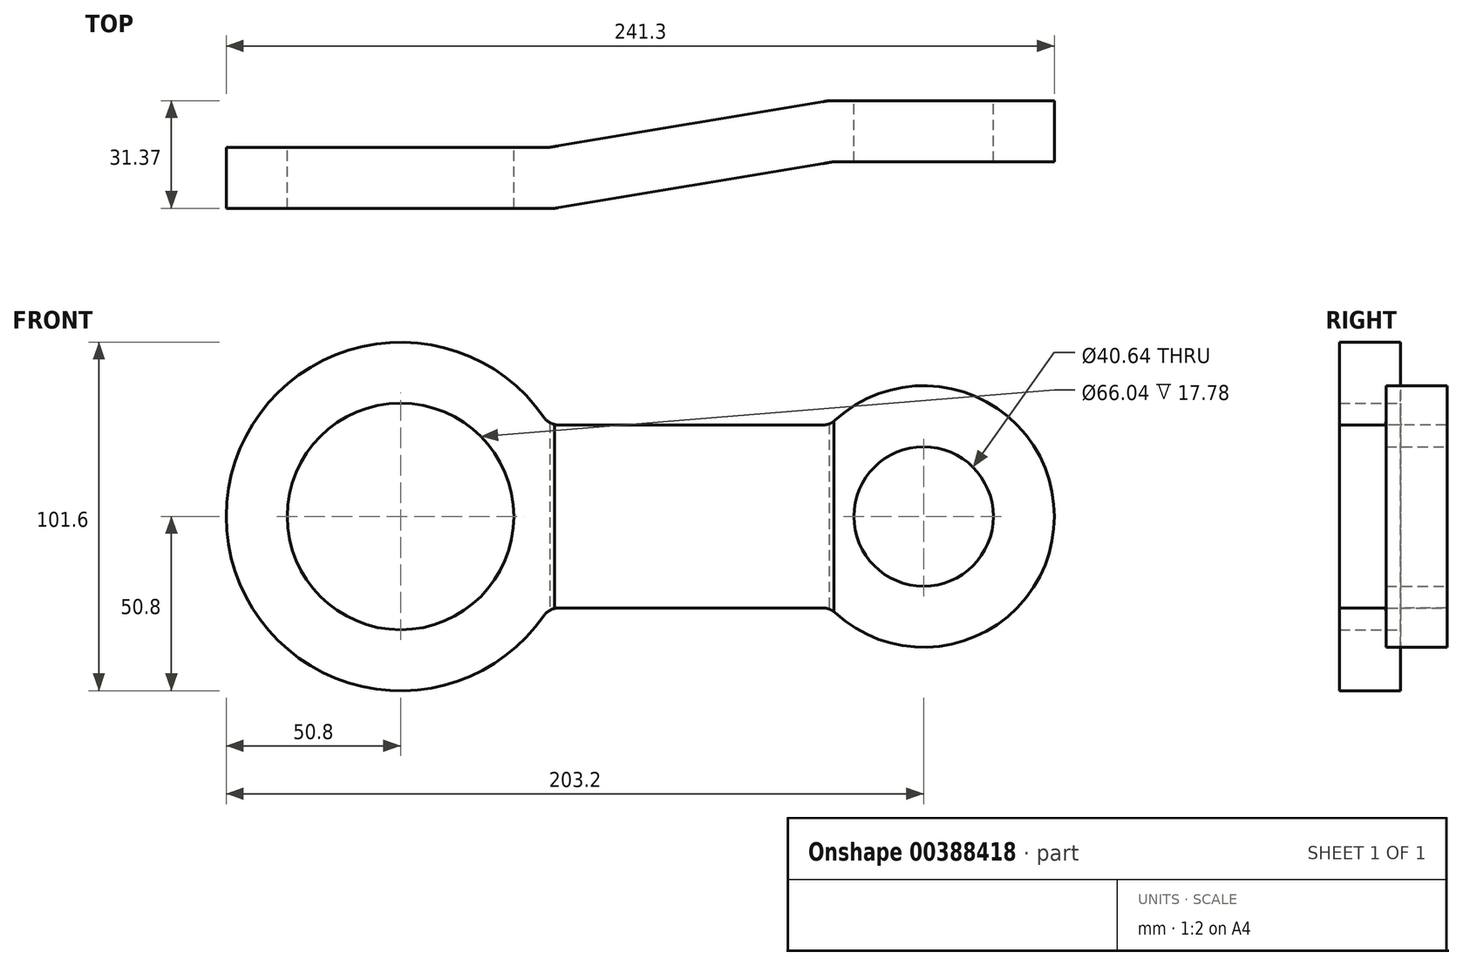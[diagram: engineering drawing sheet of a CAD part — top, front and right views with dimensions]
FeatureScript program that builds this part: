
annotation { "Feature Type Name" : "Feature", "Feature Type Description" : "" }
export const myFeature = defineFeature(function(context is Context, id is Id, definition is map)
    precondition{}
    {
        {
            var Q0;
            Q0=qCreatedBy(makeId("Front.planeOp"),FACE);
            var sketch = newSketch(context, id + "F0", { "sketchPlane" : qUnion([Q0])});
            skCircle(sketch, "E0", {"center": v(0, 0) * mm, "radius": 50.8 * mm});
            skCircle(sketch, "E1", {"center": v(152.4, 0) * mm, "radius": 38.1 * mm});
            skLineSegment(sketch, "E2", {"start": v(152.4, 0) * mm, "end": v(0, 0) * mm, "construction": true});
            skLineSegment(sketch, "E3", {"start": v(125.2, 26.67) * mm, "end": v(43.24, 26.67) * mm});
            skLineSegment(sketch, "E4.MirrorCS", {"start": v(125.2, -26.67) * mm, "end": v(43.24, -26.67) * mm});
            skCircle(sketch, "E5.0", {"center": v(152.4, 0) * mm, "radius": 20.32 * mm});
            skCircle(sketch, "E6.0", {"center": v(0, 0) * mm, "radius": 33.02 * mm});
            skSolve(sketch);
        }
        {
            var Q0;
            Q0 = qSketchRegion(id + "F0", true);
            extrude(context, id + "F1", {"entities" : qUnion([Q0]), "depth" : 50.8 * mm});
        }
        {
            var Q0;
            Q0=qCreatedBy(makeId("Top.planeOp"),FACE);
            var sketch = newSketch(context, id + "F2", { "sketchPlane" : qUnion([Q0])});
            skLineSegment(sketch, "E7", {"start": v(213.7, 0) * mm, "end": v(124.8, 0) * mm});
            skLineSegment(sketch, "E8", {"start": v(124.8, 0) * mm, "end": v(43.44, -13.59) * mm});
            skLineSegment(sketch, "E9", {"start": v(43.44, -13.59) * mm, "end": v(-83.56, -13.59) * mm});
            skLineSegment(sketch, "E10.0", {"start": v(44.92, -31.37) * mm, "end": v(-83.56, -31.37) * mm});
            skLineSegment(sketch, "E10.1", {"start": v(126.28, -17.78) * mm, "end": v(44.92, -31.37) * mm});
            skLineSegment(sketch, "E10.2", {"start": v(213.7, -17.78) * mm, "end": v(126.28, -17.78) * mm});
            skLineSegment(sketch, "E11", {"start": v(213.7, 0) * mm, "end": v(213.7, -17.78) * mm});
            skLineSegment(sketch, "E12", {"start": v(-83.56, -13.59) * mm, "end": v(-83.56, -31.37) * mm});
            skSolve(sketch);
        }
        {
            var Q0;
            Q0 = qSketchRegion(id + "F2", true);
            extrude(context, id + "F3", {"entities" : qUnion([Q0]), "operationType" : NewBodyOperationType.INTERSECT, "endBound" : BoundingType.SYMMETRIC, "depth" : 101.6 * mm});
        }
        {
            var Q0;
            Q0=makeQuery(id+"F1.opExtrude","SWEPT_EDGE",EDGE,{"disambiguationData":[OSD([sQuery(id+"F0.wireOp",EDGE,"E0"),sQuery(id+"F0.wireOp",EDGE,"E3")])]});
            fillet(context, id + "F4", {"entities" : qUnion([Q0]), "radius" : 5.08 * mm, "tangentPropagation" : true, "allowEdgeOverflow" : false});
        }
        {
            var Q0;
            Q0=makeQuery(id+"F1.opExtrude","SWEPT_EDGE",EDGE,{"disambiguationData":[OSD([sQuery(id+"F0.wireOp",EDGE,"E1"),sQuery(id+"F0.wireOp",EDGE,"E3")])]});
            fillet(context, id + "F5", {"entities" : qUnion([Q0]), "radius" : 5.08 * mm, "tangentPropagation" : true, "allowEdgeOverflow" : false});
        }
        {
            var Q0;
            Q0=makeQuery(id+"F1.opExtrude","SWEPT_EDGE",EDGE,{"disambiguationData":[OSD([sQuery(id+"F0.wireOp",EDGE,"E0"),sQuery(id+"F0.wireOp",EDGE,"E4.MirrorCS")])]});
            fillet(context, id + "F6", {"entities" : qUnion([Q0]), "radius" : 5.08 * mm, "tangentPropagation" : true, "allowEdgeOverflow" : false});
        }
        {
            var Q0;
            Q0=makeQuery(id+"F1.opExtrude","SWEPT_EDGE",EDGE,{"disambiguationData":[OSD([sQuery(id+"F0.wireOp",EDGE,"E1"),sQuery(id+"F0.wireOp",EDGE,"E4.MirrorCS")])]});
            fillet(context, id + "F7", {"entities" : qUnion([Q0]), "radius" : 5.08 * mm, "tangentPropagation" : true, "allowEdgeOverflow" : false});
        }
    });
